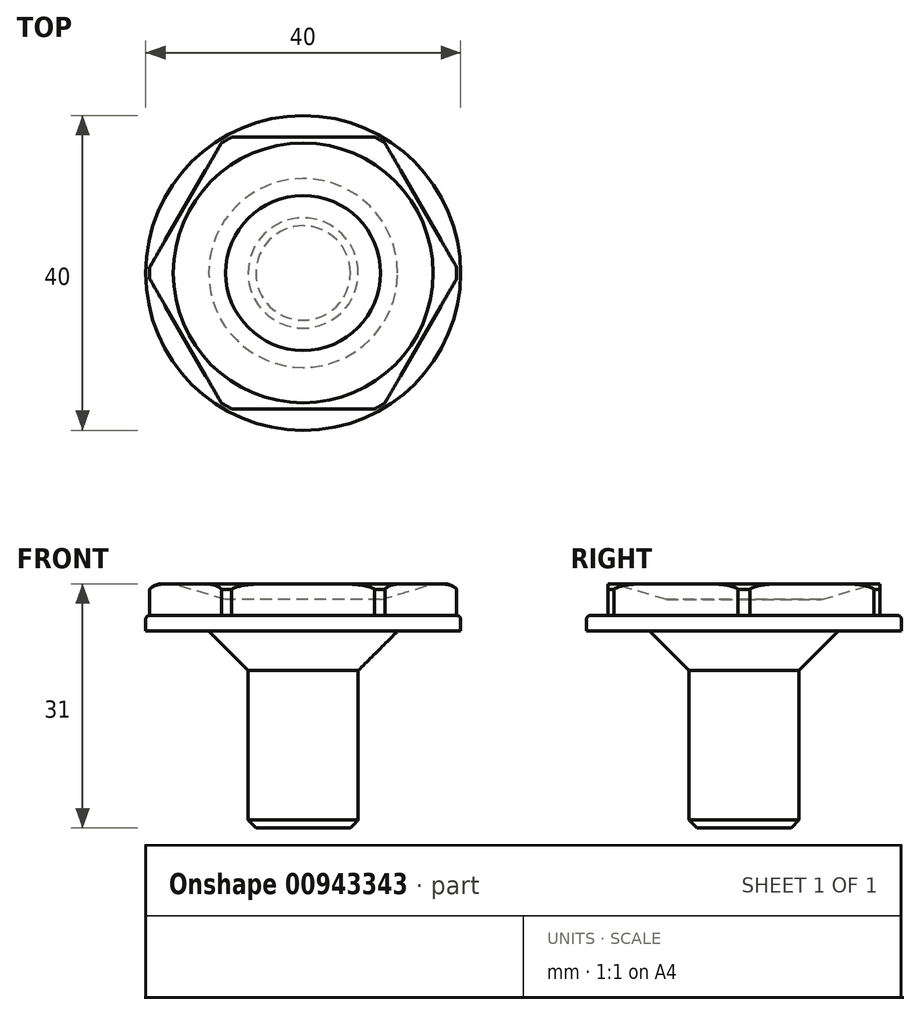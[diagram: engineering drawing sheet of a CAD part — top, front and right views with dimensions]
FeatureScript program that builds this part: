
annotation { "Feature Type Name" : "Feature", "Feature Type Description" : "" }
export const myFeature = defineFeature(function(context is Context, id is Id, definition is map)
    precondition{}
    {
        {
            var Q0;
            Q0=qCreatedBy(makeId("Top.planeOp"),FACE);
            cPlane(context, id + "F0", {"entities" : qUnion([Q0]), "cplaneType" : CPlaneType.OFFSET, "offset" : 2 * mm, "width" : 150 * mm, "height" : 150 * mm});
        }
        {
            var Q0;
            Q0=qCreatedBy(makeId("Right.planeOp"),FACE);
            var sketch = newSketch(context, id + "F1", { "sketchPlane" : qUnion([Q0])});
            skLineSegment(sketch, "E0", {"start": v(0, -25) * mm, "end": v(6, -25) * mm});
            skLineSegment(sketch, "E1", {"start": v(6, -25) * mm, "end": v(7, -24) * mm});
            skLineSegment(sketch, "E2", {"start": v(7, -24) * mm, "end": v(7, 0) * mm});
            skLineSegment(sketch, "E3", {"start": v(7, 0) * mm, "end": v(20, 0) * mm});
            skLineSegment(sketch, "E4", {"start": v(20, 0) * mm, "end": v(20, 1.5) * mm});
            skLineSegment(sketch, "E5", {"start": v(19.5, 2) * mm, "end": v(19.5, 2) * mm});
            skLineSegment(sketch, "E6", {"start": v(19.5, 2) * mm, "end": v(19.5, 5.32) * mm});
            skLineSegment(sketch, "E7", {"start": v(18, 6) * mm, "end": v(16.5, 6) * mm});
            skLineSegment(sketch, "E8", {"start": v(16.5, 6) * mm, "end": v(9.84, 4) * mm});
            skLineSegment(sketch, "E9", {"start": v(9.84, 4) * mm, "end": v(0, 4) * mm});
            skLineSegment(sketch, "E10", {"start": v(0, 4) * mm, "end": v(0, -25) * mm});
            skPoint(sketch, "E11.visualSharp", {"position": v(20, 2) * mm});
            skArc(sketch, "E11.filletArc", {"start": v(20, 1.5) * mm, "mid": v(19.85, 1.85) * mm, "end": v(19.5, 2) * mm});
            skPoint(sketch, "E12.visualSharp", {"position": v(19.5, 6) * mm});
            skArc(sketch, "E12.filletArc", {"start": v(19.5, 5.32) * mm, "mid": v(18.82, 5.82) * mm, "end": v(18, 6) * mm});
            skSolve(sketch);
        }
        {
            var Q0;
            Q0=makeQuery(id+"F1.imprint","IMPRINT",FACE,{"disambiguationData":[TD([[makeQuery(id+"F1.imprint","IMPRINT",EDGE,{"derivedFrom":sQuery(id+"F1.wireOp",EDGE,"E0")}),1.0]])]});
            var Q1;
            Q1=sQuery(id+"F1.wireOp",EDGE,"E10");
            revolve(context, id + "F2", {"surfaceOperationType" : NewSurfaceOperationType.NEW, "entities" : qUnion([Q0]), "axis" : qUnion([Q1]), "revolveType" : RevolveType.FULL});
        }
        {
            var Q0;
            Q0=qCreatedBy(id+"F0.planeOp",FACE);
            var sketch = newSketch(context, id + "F3", { "sketchPlane" : qUnion([Q0])});
            skLineSegment(sketch, "E13.0", {"start": v(-9.96, 17.25) * mm, "end": v(9.96, 17.25) * mm});
            skLineSegment(sketch, "E13.1", {"start": v(9.96, 17.25) * mm, "end": v(19.92, 0) * mm});
            skLineSegment(sketch, "E13.2", {"start": v(19.92, 0) * mm, "end": v(9.96, -17.25) * mm});
            skLineSegment(sketch, "E13.3", {"start": v(9.96, -17.25) * mm, "end": v(-9.96, -17.25) * mm});
            skLineSegment(sketch, "E13.4", {"start": v(-9.96, -17.25) * mm, "end": v(-19.92, 0) * mm});
            skLineSegment(sketch, "E13.5", {"start": v(-19.92, 0) * mm, "end": v(-9.96, 17.25) * mm});
            skCircle(sketch, "E14", {"center": v(0, 0) * mm, "radius": 21.86 * mm});
            skCircle(sketch, "E15", {"center": v(0, 0) * mm, "radius": 19.92 * mm, "construction": true});
            skSolve(sketch);
        }
        {
            var Q0;
            Q0=makeQuery(id+"F3.imprint","IMPRINT",FACE,{"disambiguationData":[TD([[makeQuery(id+"F3.imprint","IMPRINT",EDGE,{"derivedFrom":sQuery(id+"F3.wireOp",EDGE,"E13.0")}),1.0]])]});
            extrude(context, id + "F4", {"entities" : qUnion([Q0]), "operationType" : NewBodyOperationType.REMOVE, "depth" : 6 * mm, "offsetDistance" : 25 * mm});
        }
        {
            var Q0;
            Q0=makeQuery(id+"F2.opRevolve","SWEPT_EDGE",EDGE,{"disambiguationData":[OSD([sQuery(id+"F1.wireOp",EDGE,"E2"),sQuery(id+"F1.wireOp",EDGE,"E3")])]});
            chamfer(context, id + "F5", {"entities" : qUnion([Q0]), "width" : 5 * mm, "tangentPropagation" : true});
        }
    });
